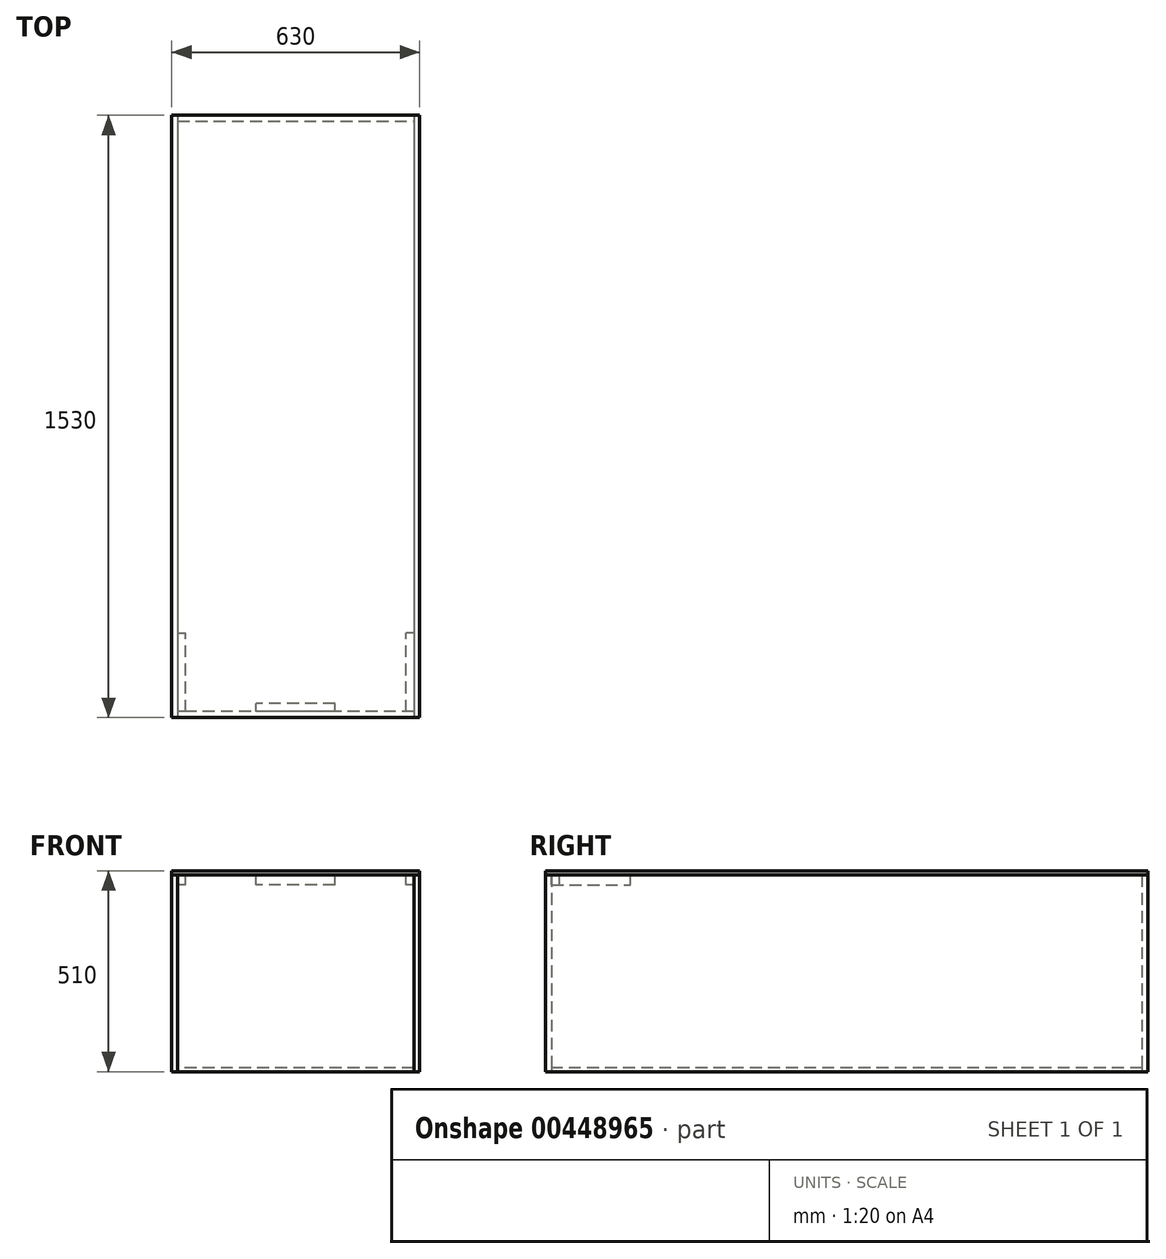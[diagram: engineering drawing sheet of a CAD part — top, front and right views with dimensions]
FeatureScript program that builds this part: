
annotation { "Feature Type Name" : "Feature", "Feature Type Description" : "" }
export const myFeature = defineFeature(function(context is Context, id is Id, definition is map)
    precondition{}
    {
        {
            var Q0;
            Q0=qCreatedBy(makeId("Top.planeOp"),FACE);
            cPlane(context, id + "F0", {"entities" : qUnion([Q0]), "cplaneType" : CPlaneType.OFFSET, "offset" : 500 * mm, "width" : 150 * mm, "height" : 150 * mm});
        }
        {
            var Q0;
            Q0=qCreatedBy(makeId("Top.planeOp"),FACE);
            var sketch = newSketch(context, id + "F1", { "sketchPlane" : qUnion([Q0])});
            skLineSegment(sketch, "E0.top", {"start": v(300, -750) * mm, "end": v(-300, -750) * mm});
            skLineSegment(sketch, "E0.left", {"start": v(300, 750) * mm, "end": v(300, -750) * mm});
            skLineSegment(sketch, "E0.right", {"start": v(-300, 750) * mm, "end": v(-300, -750) * mm});
            skPoint(sketch, "E0.middle", {"position": v(0, 0) * mm});
            skLineSegment(sketch, "E1.bottom", {"start": v(-315, 765) * mm, "end": v(-300, 765) * mm});
            skLineSegment(sketch, "E1.left", {"start": v(-315, 765) * mm, "end": v(-315, -765) * mm});
            skLineSegment(sketch, "E2", {"start": v(-382.8, 765) * mm, "end": v(-382.8, 750) * mm, "construction": true});
            skLineSegment(sketch, "E3", {"start": v(-321.03, -750) * mm, "end": v(-321.03, -765) * mm, "construction": true});
            skLineSegment(sketch, "E4", {"start": v(0, 0) * mm, "end": v(0, 632.47) * mm, "construction": true});
            skLineSegment(sketch, "E5.MirrorCS", {"start": v(315, 765) * mm, "end": v(300, 765) * mm});
            skLineSegment(sketch, "E6.MirrorCS", {"start": v(315, 765) * mm, "end": v(315, -765) * mm});
            skLineSegment(sketch, "E7", {"start": v(0, 0) * mm, "end": v(231.01, 0) * mm, "construction": true});
            skLineSegment(sketch, "E8.bottom", {"start": v(-300, 765) * mm, "end": v(300, 765) * mm});
            skLineSegment(sketch, "E8.top", {"start": v(-300, 750) * mm, "end": v(300, 750) * mm});
            skLineSegment(sketch, "E8.left", {"start": v(-300, 765) * mm, "end": v(-300, 750) * mm});
            skLineSegment(sketch, "E8.right", {"start": v(300, 765) * mm, "end": v(300, 750) * mm});
            skLineSegment(sketch, "E9", {"start": v(-315, -765) * mm, "end": v(315, -765) * mm});
            skLineSegment(sketch, "E10", {"start": v(300, -750) * mm, "end": v(300, -765) * mm});
            skLineSegment(sketch, "E11", {"start": v(-300, -750) * mm, "end": v(-300, -765) * mm});
            skLineSegment(sketch, "E12", {"start": v(-300, -750) * mm, "end": v(-315, -750) * mm, "construction": true});
            skSolve(sketch);
        }
        {
            var Q0;
            Q0=makeQuery(id+"F1.imprint","IMPRINT",FACE,{"disambiguationData":[TD([[makeQuery(id+"F1.imprint","IMPRINT",EDGE,{"derivedFrom":sQuery(id+"F1.wireOp",EDGE,"E0.top")}),-1.0]])]});
            extrude(context, id + "F2", {"entities" : qUnion([Q0]), "depth" : 10 * mm});
        }
        {
            var Q0;
            Q0=makeQuery(id+"F1.imprint","IMPRINT",FACE,{"disambiguationData":[TD([[makeQuery(id+"F1.imprint","IMPRINT",EDGE,{"derivedFrom":sQuery(id+"F1.wireOp",EDGE,"E8.bottom")}),-1.0]])]});
            var Q1;
            Q1=qCreatedBy(id+"F0.planeOp",FACE);
            extrude(context, id + "F3", {"entities" : qUnion([Q0]), "endBound" : BoundingType.UP_TO_SURFACE, "endBoundEntityFace" : qUnion([Q1]), "depth" : 25 * mm});
        }
        {
            var Q0;
            Q0=makeQuery(id+"F1.imprint","IMPRINT",FACE,{"disambiguationData":[TD([[makeQuery(id+"F1.imprint","IMPRINT",EDGE,{"derivedFrom":sQuery(id+"F1.wireOp",EDGE,"E0.top")}),1.0]])]});
            var Q1;
            Q1=qCreatedBy(id+"F0.planeOp",FACE);
            extrude(context, id + "F4", {"entities" : qUnion([Q0]), "endBound" : BoundingType.UP_TO_SURFACE, "endBoundEntityFace" : qUnion([Q1]), "depth" : 25 * mm});
        }
        {
            var Q0;
            Q0=makeQuery(id+"F1.imprint","IMPRINT",FACE,{"disambiguationData":[TD([[makeQuery(id+"F1.imprint","IMPRINT",EDGE,{"derivedFrom":sQuery(id+"F1.wireOp",EDGE,"E0.left")}),1.0]])]});
            var Q1;
            Q1=qCreatedBy(id+"F0.planeOp",FACE);
            extrude(context, id + "F5", {"entities" : qUnion([Q0]), "endBound" : BoundingType.UP_TO_SURFACE, "endBoundEntityFace" : qUnion([Q1]), "depth" : 25 * mm});
        }
        {
            var Q0;
            Q0=makeQuery(id+"F1.imprint","IMPRINT",FACE,{"disambiguationData":[TD([[makeQuery(id+"F1.imprint","IMPRINT",EDGE,{"derivedFrom":sQuery(id+"F1.wireOp",EDGE,"E0.right")}),-1.0]])]});
            var Q1;
            Q1=qCreatedBy(id+"F0.planeOp",FACE);
            extrude(context, id + "F6", {"entities" : qUnion([Q0]), "endBound" : BoundingType.UP_TO_SURFACE, "endBoundEntityFace" : qUnion([Q1]), "depth" : 25 * mm});
        }
        {
            var Q0;
            Q0=qCreatedBy(id+"F0.planeOp",FACE);
            var sketch = newSketch(context, id + "F7", { "sketchPlane" : qUnion([Q0])});
            skPoint(sketch, "E13.0", {"position": v(-315, 765) * mm});
            skPoint(sketch, "E14.0", {"position": v(315, 765) * mm});
            skPoint(sketch, "E15.0", {"position": v(-315, -765) * mm});
            skPoint(sketch, "E16.0", {"position": v(315, -765) * mm});
            skLineSegment(sketch, "E17", {"start": v(315, -765) * mm, "end": v(-315, -765) * mm});
            skLineSegment(sketch, "E18", {"start": v(-315, -765) * mm, "end": v(-315, 765) * mm});
            skLineSegment(sketch, "E19", {"start": v(-315, 765) * mm, "end": v(315, 765) * mm});
            skLineSegment(sketch, "E20", {"start": v(315, 765) * mm, "end": v(315, -765) * mm});
            skSolve(sketch);
        }
        {
            var Q0;
            Q0=makeQuery(id+"F7.imprint","IMPRINT",FACE,{"disambiguationData":[TD([[makeQuery(id+"F7.imprint","IMPRINT",EDGE,{"derivedFrom":sQuery(id+"F7.wireOp",EDGE,"E17")}),-1.0]])]});
            extrude(context, id + "F8", {"entities" : qUnion([Q0]), "depth" : 10 * mm});
        }
        {
            var Q0;
            Q0=qCreatedBy(id+"F0.planeOp",FACE);
            var sketch = newSketch(context, id + "F9", { "sketchPlane" : qUnion([Q0])});
            skLineSegment(sketch, "E21.0", {"start": v(-300, 750) * mm, "end": v(300, 750) * mm});
            skLineSegment(sketch, "E22.0", {"start": v(300, 750) * mm, "end": v(300, -750) * mm});
            skLineSegment(sketch, "E23.0", {"start": v(-300, 750) * mm, "end": v(-300, -750) * mm});
            skLineSegment(sketch, "E24.bottom", {"start": v(100, 750) * mm, "end": v(-100, 750) * mm});
            skLineSegment(sketch, "E24.top", {"start": v(100, 730) * mm, "end": v(-100, 730) * mm});
            skLineSegment(sketch, "E24.left", {"start": v(100, 750) * mm, "end": v(100, 730) * mm});
            skLineSegment(sketch, "E24.right", {"start": v(-100, 750) * mm, "end": v(-100, 730) * mm});
            skLineSegment(sketch, "E25", {"start": v(0, 730) * mm, "end": v(0, 750) * mm, "construction": true});
            skLineSegment(sketch, "E26.bottom", {"start": v(300, 750) * mm, "end": v(280, 750) * mm});
            skLineSegment(sketch, "E26.top", {"start": v(300, 550) * mm, "end": v(280, 550) * mm});
            skLineSegment(sketch, "E26.left", {"start": v(300, 750) * mm, "end": v(300, 550) * mm});
            skLineSegment(sketch, "E26.right", {"start": v(280, 750) * mm, "end": v(280, 550) * mm});
            skLineSegment(sketch, "E27.bottom", {"start": v(-300, 750) * mm, "end": v(-280, 750) * mm});
            skLineSegment(sketch, "E27.top", {"start": v(-300, 550) * mm, "end": v(-280, 550) * mm});
            skLineSegment(sketch, "E27.left", {"start": v(-300, 750) * mm, "end": v(-300, 550) * mm});
            skLineSegment(sketch, "E27.right", {"start": v(-280, 750) * mm, "end": v(-280, 550) * mm});
            skLineSegment(sketch, "E28.0", {"start": v(0, 0) * mm, "end": v(231.01, 0) * mm, "construction": true});
            skLineSegment(sketch, "E29.MirrorCS", {"start": v(-280, -750) * mm, "end": v(-280, -550) * mm});
            skLineSegment(sketch, "E30.MirrorCS", {"start": v(-300, -550) * mm, "end": v(-280, -550) * mm});
            skLineSegment(sketch, "E31.MirrorCS", {"start": v(100, -750) * mm, "end": v(100, -730) * mm});
            skLineSegment(sketch, "E32.MirrorCS", {"start": v(100, -730) * mm, "end": v(-100, -730) * mm});
            skLineSegment(sketch, "E33.MirrorCS", {"start": v(-100, -750) * mm, "end": v(-100, -730) * mm});
            skLineSegment(sketch, "E34.MirrorCS", {"start": v(280, -750) * mm, "end": v(280, -550) * mm});
            skLineSegment(sketch, "E35.MirrorCS", {"start": v(300, -550) * mm, "end": v(280, -550) * mm});
            skLineSegment(sketch, "E36.0", {"start": v(300, -750) * mm, "end": v(-300, -750) * mm});
            skSolve(sketch);
        }
        {
            var Q0;
            {var subQ4=sQuery(id+"F9.wireOp",EDGE,"E34.MirrorCS");Q0=makeQuery(id+"F9.imprint","IMPRINT",FACE,{"disambiguationData":[TD([[makeQuery(id+"F9.imprint","IMPRINT",EDGE,{"derivedFrom":subQ4}),-1.0]])]});}
            extrude(context, id + "F10", {"entities" : qUnion([Q0]), "oppositeDirection" : true, "depth" : 25 * mm});
        }
        {
            var Q0;
            {var subQ0=sQuery(id+"F9.wireOp",EDGE,"E31.MirrorCS");Q0=makeQuery(id+"F9.imprint","IMPRINT",FACE,{"disambiguationData":[TD([[makeQuery(id+"F9.imprint","IMPRINT",EDGE,{"derivedFrom":subQ0}),1.0]])]});}
            var Q1;
            {var subQ4=sQuery(id+"F9.wireOp",EDGE,"E29.MirrorCS");Q1=makeQuery(id+"F9.imprint","IMPRINT",FACE,{"disambiguationData":[TD([[makeQuery(id+"F9.imprint","IMPRINT",EDGE,{"derivedFrom":subQ4}),1.0]])]});}
            var Q2;
            Q2=makeQuery(id+"F9.imprint","IMPRINT",FACE,{"disambiguationData":[TD([[makeQuery(id+"F9.imprint","IMPRINT",EDGE,{"derivedFrom":sQuery(id+"F9.wireOp",EDGE,"E26.bottom")}),1.0]])]});
            var Q3;
            Q3=makeQuery(id+"F9.imprint","IMPRINT",FACE,{"disambiguationData":[TD([[makeQuery(id+"F9.imprint","IMPRINT",EDGE,{"derivedFrom":sQuery(id+"F9.wireOp",EDGE,"E24.bottom")}),1.0]])]});
            var Q4;
            Q4=makeQuery(id+"F9.imprint","IMPRINT",FACE,{"disambiguationData":[TD([[makeQuery(id+"F9.imprint","IMPRINT",EDGE,{"derivedFrom":sQuery(id+"F9.wireOp",EDGE,"E27.bottom")}),-1.0]])]});
            extrude(context, id + "F11", {"entities" : qUnion([Q0, Q1, Q2, Q3, Q4]), "oppositeDirection" : true, "depth" : 25 * mm});
        }
    });
